# Revit family: 1302a_omni_us
name_source: partatom
category: Communication Devices
units: mm (PartAtom-declared; Revit-internal decimal feet)

## family parameters
Cut with Voids When Loaded = No
Host = Face
Maintain Annotation Orientation = No
OmniClass Number = 23.85.80.11.27
OmniClass Title = Lighting Controls
Part Type = Normal
Room Calculation Point = No
Round Connector Dimension = Use Diameter
Shared = Yes

## types (1)
- 1302a_omni_us
    Assembly Code = D5090
    Certifications = UL and cUL listed
    Coverage = 500 - 2000 sq ft, based on model
    Default Elevation = 48 "
    Description = The OMNIUS uses ultrasonic (US) technology to turn lighting on and off based on
occupancy. Designed specifically for both areas with obstructions (e.g. columns,
cubicles, stalls, and filing cabinets) and areas with long periods of minor-motion
activity (e.g. typing), this sensor features  Controls' patented IntelliDAPT®
technology, which makes all the sensor adjustments automatically.
    Features = IntelliDAPT self-adaptive technology - no manual adjustment required 
Superior all-digital ultrasonic (US) minor motion detection 
Non-volatile memory for sensor settings  
500–2,000 square-foot coverage area (depending on model) 
Optional relay and photocell control 
Optional Quick to Install (QTI) connector 
UL and cUL listed 
California Title 24 compliant
Five-year limited warranty 
Low Voltage 24 Vdc
    Housing Material = Paint - Matte White
    Manufacturer = NX Lighting Controls
    Model = OMNI® Low Voltage Ultrasonic Ceiling Sensor
    Power Requirements = 24VDC, 33mA (uses UVPP and MP- Series power pack- not included)
    Sensing Element = Metal-Nickel
    Type Comments = OMNI® Low Voltage Dual Technology Ultrasonic and PIR
    URL = https://www.currentlighting.com
    Warranty = 5-Years Warranty
    Width = 4.5 "

## geometry (parser evidence)
native form markers: Sweep x2
no freeform markers — native parametric forms only
